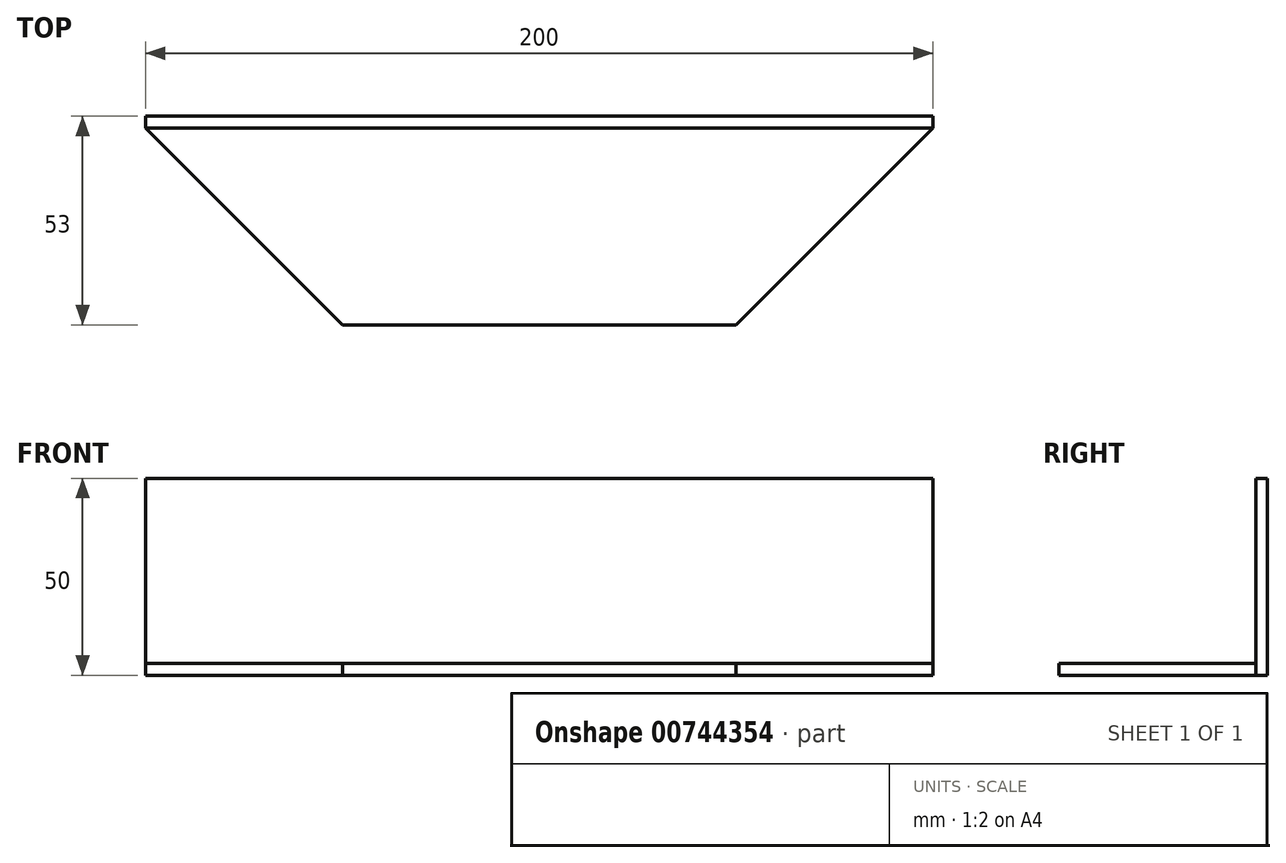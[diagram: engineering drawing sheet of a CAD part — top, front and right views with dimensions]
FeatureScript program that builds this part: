
annotation { "Feature Type Name" : "Feature", "Feature Type Description" : "" }
export const myFeature = defineFeature(function(context is Context, id is Id, definition is map)
    precondition{}
    {
        {
            var Q0;
            Q0=qCreatedBy(makeId("Top.planeOp"),FACE);
            var sketch = newSketch(context, id + "F0", { "sketchPlane" : qUnion([Q0])});
            skLineSegment(sketch, "E0.bottom", {"start": v(50, -25) * mm, "end": v(-50, -25) * mm});
            skLineSegment(sketch, "E0.top", {"start": v(100, 25) * mm, "end": v(-100, 25) * mm});
            skPoint(sketch, "E0.middle", {"position": v(0, 0) * mm});
            skLineSegment(sketch, "E1", {"start": v(0, 0) * mm, "end": v(0, -25) * mm});
            skLineSegment(sketch, "E2", {"start": v(0, -25) * mm, "end": v(-50, -25) * mm});
            skLineSegment(sketch, "E3", {"start": v(-50, -25) * mm, "end": v(50, -25) * mm});
            skLineSegment(sketch, "E4", {"start": v(-50, -25) * mm, "end": v(-100, 25) * mm});
            skLineSegment(sketch, "E5", {"start": v(50, -25) * mm, "end": v(100, 25) * mm});
            skPoint(sketch, "E0.right.start.orphan", {"position": v(-100, -25) * mm});
            skPoint(sketch, "E0.left.start.orphan", {"position": v(100, -25) * mm});
            skLineSegment(sketch, "E6", {"start": v(-100, 25) * mm, "end": v(-100, 28) * mm});
            skLineSegment(sketch, "E7", {"start": v(100, 25) * mm, "end": v(100, 28) * mm});
            skLineSegment(sketch, "E8", {"start": v(100, 28) * mm, "end": v(-100, 28) * mm});
            skSolve(sketch);
        }
        {
            var Q0;
            Q0=makeQuery(id+"F0.imprint","IMPRINT",FACE,{"disambiguationData":[TD([[makeQuery(id+"F0.imprint","IMPRINT",EDGE,{"derivedFrom":sQuery(id+"F0.wireOp",EDGE,"E0.top")}),-1.0]])]});
            extrude(context, id + "F1", {"entities" : qUnion([Q0]), "depth" : 50 * mm, "offsetDistance" : 25 * mm});
        }
        {
            var Q0;
            Q0=makeQuery(id+"F0.imprint","IMPRINT",FACE,{"disambiguationData":[TD([[makeQuery(id+"F0.imprint","IMPRINT",EDGE,{"derivedFrom":sQuery(id+"F0.wireOp",EDGE,"E0.top")}),1.0]])]});
            extrude(context, id + "F2", {"entities" : qUnion([Q0]), "operationType" : NewBodyOperationType.ADD, "depth" : 3 * mm, "offsetDistance" : 25 * mm});
        }
    });
